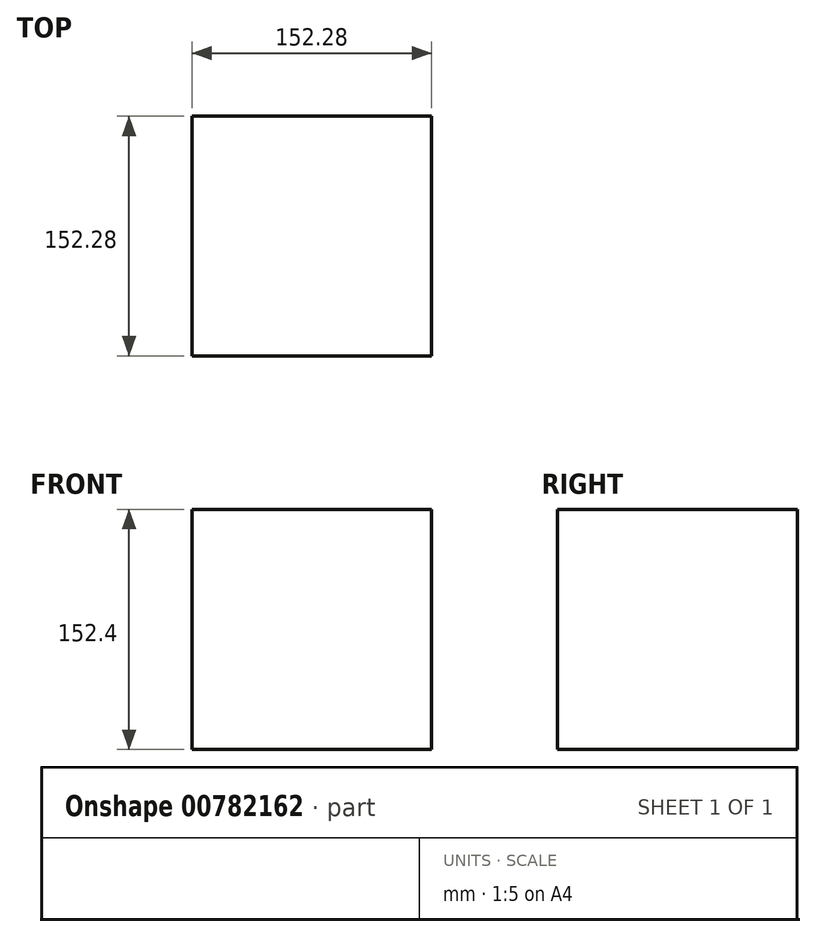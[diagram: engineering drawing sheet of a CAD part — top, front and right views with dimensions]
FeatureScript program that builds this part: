
annotation { "Feature Type Name" : "Feature", "Feature Type Description" : "" }
export const myFeature = defineFeature(function(context is Context, id is Id, definition is map)
    precondition{}
    {
        {
            var Q0;
            Q0=qCreatedBy(makeId("Top.planeOp"),FACE);
            var sketch = newSketch(context, id + "F0", { "sketchPlane" : qUnion([Q0])});
            skLineSegment(sketch, "E0.bottom", {"start": v(-76, 76.53) * mm, "end": v(76.27, 76.53) * mm});
            skLineSegment(sketch, "E0.top", {"start": v(-76, -75.75) * mm, "end": v(76.27, -75.75) * mm});
            skLineSegment(sketch, "E0.left", {"start": v(-76, 76.53) * mm, "end": v(-76, -75.75) * mm});
            skLineSegment(sketch, "E0.right", {"start": v(76.27, 76.53) * mm, "end": v(76.27, -75.75) * mm});
            skSolve(sketch);
        }
        {
            var Q0;
            Q0=makeQuery(id+"F0.imprint","IMPRINT",FACE,{"disambiguationData":[TD([[makeQuery(id+"F0.imprint","IMPRINT",EDGE,{"derivedFrom":sQuery(id+"F0.wireOp",EDGE,"E0.bottom")}),-1.0]])]});
            extrude(context, id + "F1", {"entities" : qUnion([Q0]), "depth" : 152.4 * mm, "offsetDistance" : 25.4 * mm});
        }
    });
